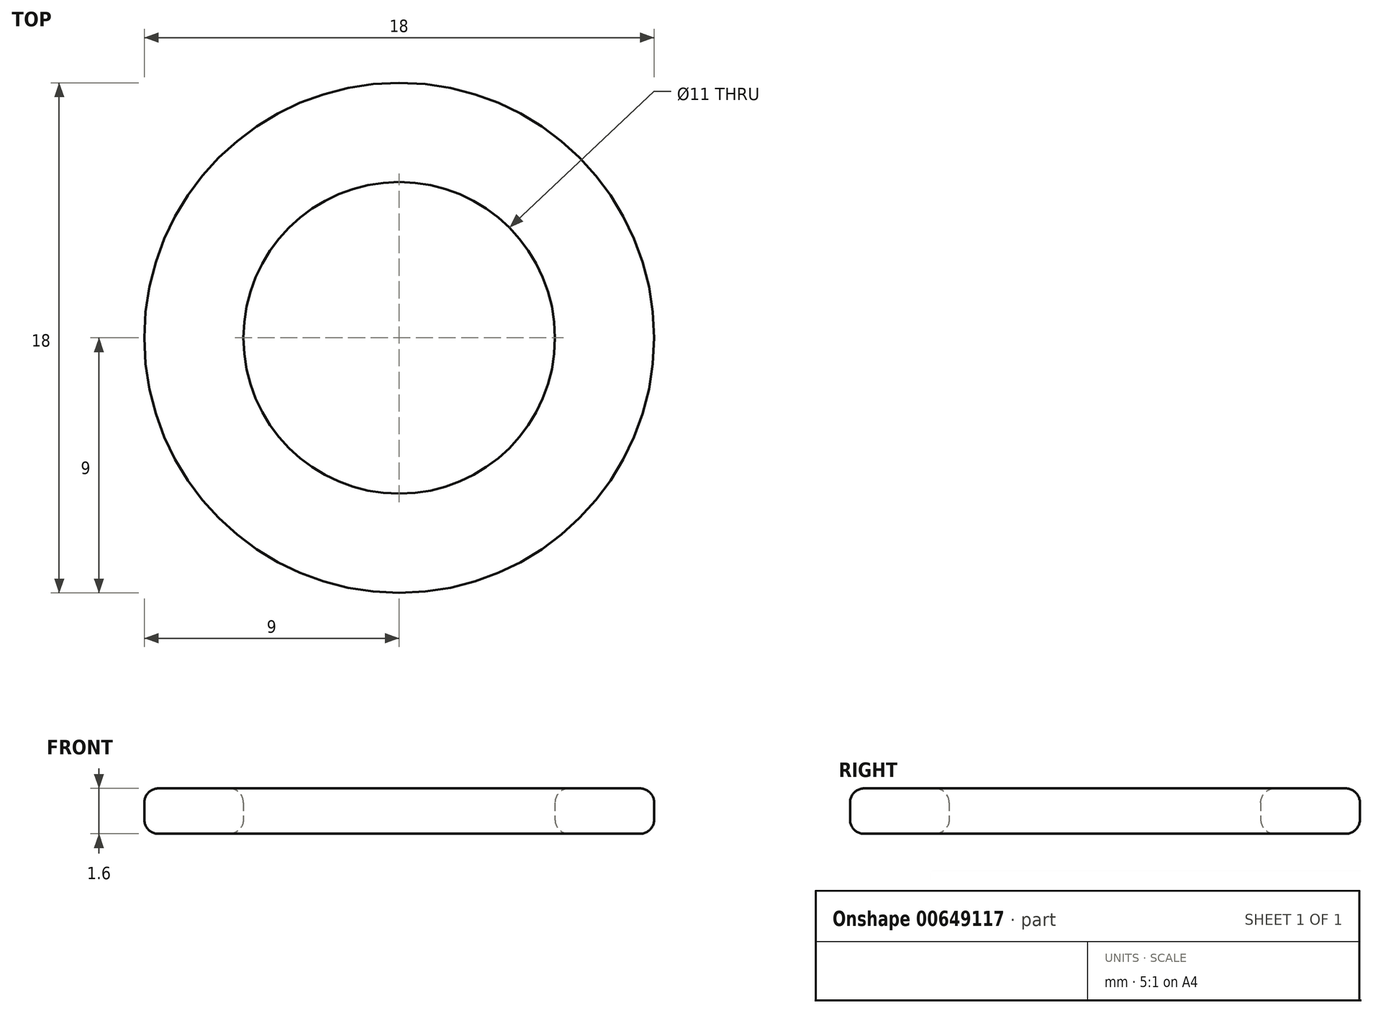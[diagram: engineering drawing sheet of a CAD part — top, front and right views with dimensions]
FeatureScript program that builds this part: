
annotation { "Feature Type Name" : "Feature", "Feature Type Description" : "" }
export const myFeature = defineFeature(function(context is Context, id is Id, definition is map)
    precondition{}
    {
        {
            var Q0;
            Q0=qCreatedBy(makeId("Top.planeOp"),FACE);
            var sketch = newSketch(context, id + "F0", { "sketchPlane" : qUnion([Q0])});
            skCircle(sketch, "E0", {"center": v(0, 0) * mm, "radius": 9 * mm});
            skCircle(sketch, "E1", {"center": v(0, 0) * mm, "radius": 5.5 * mm});
            skSolve(sketch);
        }
        {
            var Q0;
            Q0=makeQuery(id+"F0.imprint","IMPRINT",FACE,{"disambiguationData":[TD([[makeQuery(id+"F0.imprint","IMPRINT",EDGE,{"derivedFrom":sQuery(id+"F0.wireOp",EDGE,"E0")}),1.0]])]});
            extrude(context, id + "F1", {"entities" : qUnion([Q0]), "depth" : 1.6 * mm, "offsetDistance" : 25 * mm});
        }
        {
            var Q0;
            Q0=makeQuery(id+"F1.opExtrude","CAP_EDGE",EDGE,{"disambiguationData":[OSD([sQuery(id+"F0.wireOp",EDGE,"E0")])],"isStart":false});
            var Q1;
            Q1=makeQuery(id+"F1.opExtrude","CAP_EDGE",EDGE,{"disambiguationData":[OSD([sQuery(id+"F0.wireOp",EDGE,"E1")])],"isStart":false});
            var Q2;
            Q2=makeQuery(id+"F1.opExtrude","CAP_EDGE",EDGE,{"disambiguationData":[OSD([sQuery(id+"F0.wireOp",EDGE,"E0")])],"isStart":true});
            var Q3;
            Q3=makeQuery(id+"F1.opExtrude","CAP_EDGE",EDGE,{"disambiguationData":[OSD([sQuery(id+"F0.wireOp",EDGE,"E1")])],"isStart":true});
            fillet(context, id + "F2", {"entities" : qUnion([Q0, Q1, Q2, Q3]), "radius" : 0.5 * mm, "tangentPropagation" : true, "allowEdgeOverflow" : false});
        }
    });
